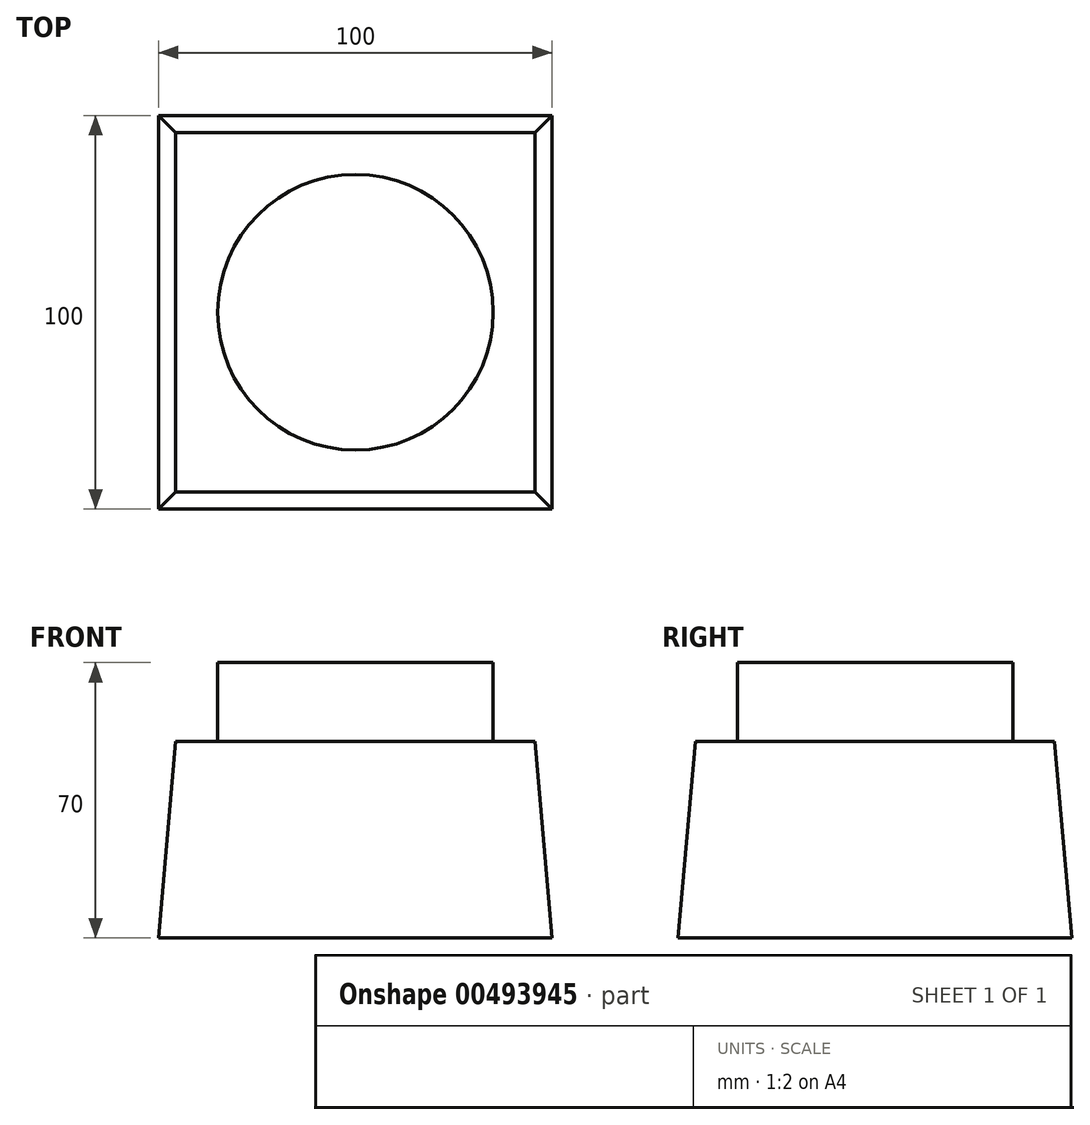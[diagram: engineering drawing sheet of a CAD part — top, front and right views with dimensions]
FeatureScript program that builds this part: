
annotation { "Feature Type Name" : "Feature", "Feature Type Description" : "" }
export const myFeature = defineFeature(function(context is Context, id is Id, definition is map)
    precondition{}
    {
        {
            var Q0;
            Q0=qCreatedBy(makeId("Top.planeOp"),FACE);
            var sketch = newSketch(context, id + "F0", { "sketchPlane" : qUnion([Q0])});
            skLineSegment(sketch, "E0.bottom", {"start": v(-50, 50) * mm, "end": v(50, 50) * mm});
            skLineSegment(sketch, "E0.top", {"start": v(-50, -50) * mm, "end": v(50, -50) * mm});
            skLineSegment(sketch, "E0.left", {"start": v(-50, 50) * mm, "end": v(-50, -50) * mm});
            skLineSegment(sketch, "E0.right", {"start": v(50, 50) * mm, "end": v(50, -50) * mm});
            skPoint(sketch, "E0.middle", {"position": v(0, 0) * mm});
            skSolve(sketch);
        }
        {
            var Q0;
            Q0=makeQuery(id+"F0.imprint","IMPRINT",FACE,{"disambiguationData":[TD([[makeQuery(id+"F0.imprint","IMPRINT",EDGE,{"derivedFrom":sQuery(id+"F0.wireOp",EDGE,"E0.bottom")}),-1.0]])]});
            extrude(context, id + "F1", {"entities" : qUnion([Q0]), "depth" : 50 * mm, "hasDraft" : true, "draftAngle" : 5 * degree, "draftPullDirection" : true});
        }
        {
            var Q0;
            Q0=makeQuery(id+"F1.opExtrude","CAP_FACE",FACE,{"disambiguationData":[OSD([sQuery(id+"F0.wireOp",EDGE,"E0.bottom"),sQuery(id+"F0.wireOp",EDGE,"E0.top"),sQuery(id+"F0.wireOp",EDGE,"E0.left"),sQuery(id+"F0.wireOp",EDGE,"E0.right")])],"isStart":false});
            var sketch = newSketch(context, id + "F2", { "sketchPlane" : qUnion([Q0])});
            skCircle(sketch, "E1", {"center": v(0, 0) * mm, "radius": 35 * mm});
            skSolve(sketch);
        }
        {
            var Q0;
            Q0 = qSketchRegion(id + "F2", true);
            extrude(context, id + "F3", {"entities" : qUnion([Q0]), "operationType" : NewBodyOperationType.ADD, "depth" : 20 * mm});
        }
    });
